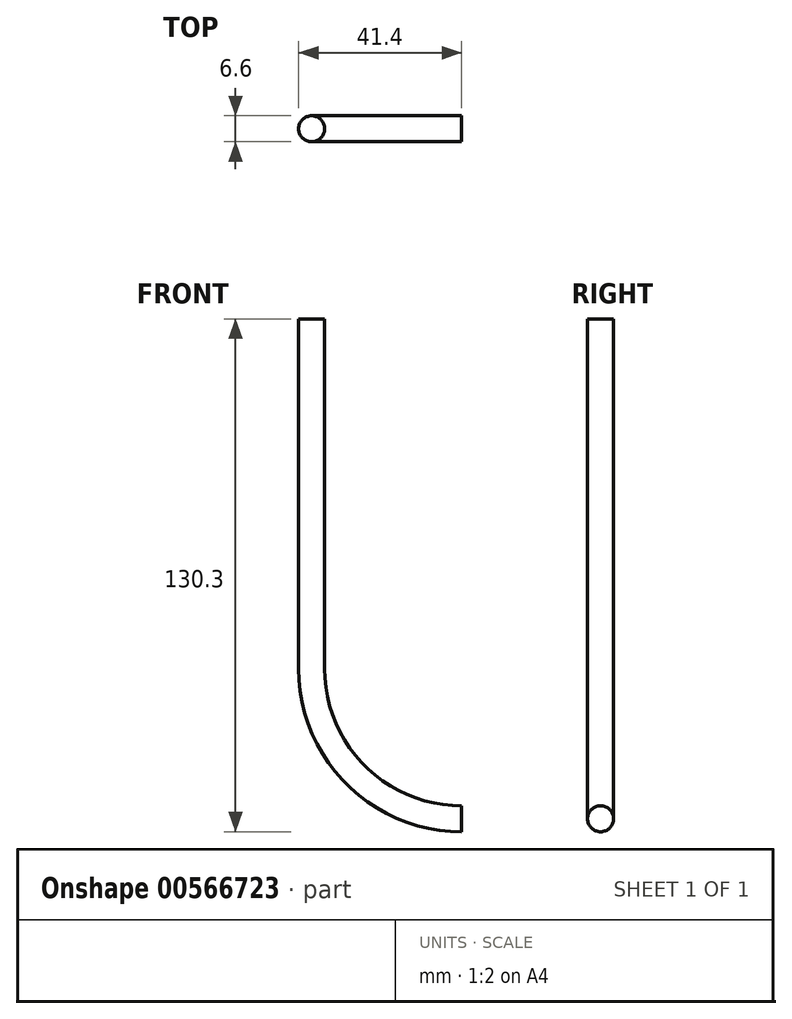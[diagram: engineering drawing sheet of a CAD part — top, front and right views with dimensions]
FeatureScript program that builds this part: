
annotation { "Feature Type Name" : "Feature", "Feature Type Description" : "" }
export const myFeature = defineFeature(function(context is Context, id is Id, definition is map)
    precondition{}
    {
        {
            var Q0;
            Q0=qCreatedBy(makeId("Top.planeOp"),FACE);
            var sketch = newSketch(context, id + "F0", { "sketchPlane" : qUnion([Q0])});
            skPoint(sketch, "E0", {"position": v(-38.1, 0) * mm});
            skSolve(sketch);
        }
        {
            var Q0;
            Q0=qCreatedBy(makeId("Top.planeOp"),FACE);
            var sketch = newSketch(context, id + "F1", { "sketchPlane" : qUnion([Q0])});
            skCircle(sketch, "E1", {"center": v(-38.1, 0) * mm, "radius": 3.3 * mm});
            skSolve(sketch);
        }
        {
            var Q0;
            Q0=qCreatedBy(makeId("Top.planeOp"),FACE);
            var sketch = newSketch(context, id + "F2", { "sketchPlane" : qUnion([Q0])});
            skLineSegment(sketch, "E2", {"start": v(0, 29.94) * mm, "end": v(0, -26.76) * mm});
            skSolve(sketch);
        }
        {
            var Q0;
            Q0=makeQuery(id+"F1.imprint","IMPRINT",FACE,{"disambiguationData":[TD([[makeQuery(id+"F1.imprint","IMPRINT",EDGE,{"derivedFrom":sQuery(id+"F1.wireOp",EDGE,"E1")}),1.0]])]});
            var Q1;
            Q1=sQuery(id+"F2.wireOp",EDGE,"E2");
            revolve(context, id + "F3", {"surfaceOperationType" : NewSurfaceOperationType.NEW, "entities" : qUnion([Q0]), "axis" : qUnion([Q1]), "revolveType" : RevolveType.ONE_DIRECTION, "angle" : 90 * degree});
        }
        {
            var Q0;
            Q0=makeQuery(id+"F3.opRevolve","CAP_FACE",FACE,{"disambiguationData":[OSD([sQuery(id+"F1.wireOp",EDGE,"E1")])],"isStart":true});
            extrude(context, id + "F4", {"entities" : qUnion([Q0]), "operationType" : NewBodyOperationType.ADD, "depth" : 88.9 * mm, "offsetDistance" : 25.4 * mm});
        }
    });
